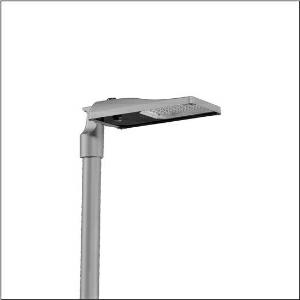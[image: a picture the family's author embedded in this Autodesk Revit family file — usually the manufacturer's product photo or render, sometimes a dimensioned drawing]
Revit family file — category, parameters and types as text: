
# Revit family: streetlight_sl_31_mini___st1_0a_5xh6d71t08ha_56cc
name_source: partatom
category: Lighting Fixtures
units: mm (PartAtom-declared; Revit-internal decimal feet)

## family parameters
Cut with Voids When Loaded = No
Host = Face
Light Source = No
Part Type = Normal
Room Calculation Point = No
Round Connector Dimension = Use Diameter
Shared = No

## types (1)
- --- (1 x LED, 7460 lm, 68.3 W, 2200K)
    Apparent Load = 68 VA
    CIE Flux Codes = 37 72 97 100 100
    Color Rendering = 70
    Color Temperature = 2200K
    Default Elevation = 1800 mm
    Description = Streetlight SL 31 mini D4i, Desk-Remote mast luminaire for post-top, side-entry; light control with lens of PMMA; light distribution: ST1.0a, direct asymmetric distribution, for standard-compliant lighting for roads and squares; LED: luminous flux: 7.460lm, light colour: 722, colour temperature: 2200K; luminous efficacy: 109,2lm/W; control: pre-setting: logarithmic dimming characteristic, flexible luminous flux parameterisation, time-dependent luminous flux control, constant luminous flux control, power reduction, intelligent temperature release in ECG and LED module, overheat protection; luminaire housing, of diecast aluminium, SITECO metallic grey (DB 702S), corrosivity category C5 high according to DIN EN ISO 12944; cover of toughened safety glass, transparent, opened without tools; mast flange of diecast aluminium, SITECO metallic grey (DB 702S), spigot size: 76/60mm, mast flange included unmounted; cable length: 8,5m, connection cable pre-assembled; mains connection: 220..240V, AC, 50/60Hz; power consumption (at start of service life): 68,3W / (at end of service life): 74,5W / (with reduced operation 50%): 29,2W; protection rating (complete): IP66; insulation class (complete): insulation class II (safety insulation); impact resistance: IK09; certification: CE, ENEC, ENEC+, VDE, UKCA, ZD4i; permissible operating ambient temperature for outdoor applications: -40..+50°C; packaging unit: 1 piece

Light Distribution: ST1.0a
    Height = 76 mm
    Lamp = 1 x LED
    Lamp Light Flux = 7460 lm
    Lamp Power = 68.3 W
    Lamp count = 1
    Length = 547 mm
    Luminous efficacy = 109 lm/W
    Manufacturer = Siteco
    ModVariant = No
    Model = 5XH6D71T08HA
    Number of Poles = 1
    OnlyDefault = Yes
    Power Factor = 1
    Product Name = Streetlight SL 31 mini | ST1.0a
    Product group = mast luminaire | pylon top
    ProductGroupID = 6100
    Protection Class = Protection class II
    Protection Degree = IP 66
    RLX_Detail_Level = 1
    RLX_Emergency_Light_Flux = 0 lm
    RLX_Emergency_Type = 0
    RLX_Emergency_Type_DB = No
    RlxData = <blob elided: 24265 chars, md5=42878217>
    Socket = socket
    Standby Power = 0 W
    System Light Flux = 7460 lm
    System Power = 68 W
    Type Comments = factory setting: luminous flux: 100 % | dim-lin: 254 | 692 mA
    Type Image = l_1300332.jpg
    URL = http://relux.com
    VarID = @adj_009283
    Voltage = 0 V
    Weight = 0.00 kg
    Width = 265 mm

## geometry (parser evidence)
native form markers: Blend x4, Sweep x9
no freeform markers — native parametric forms only
